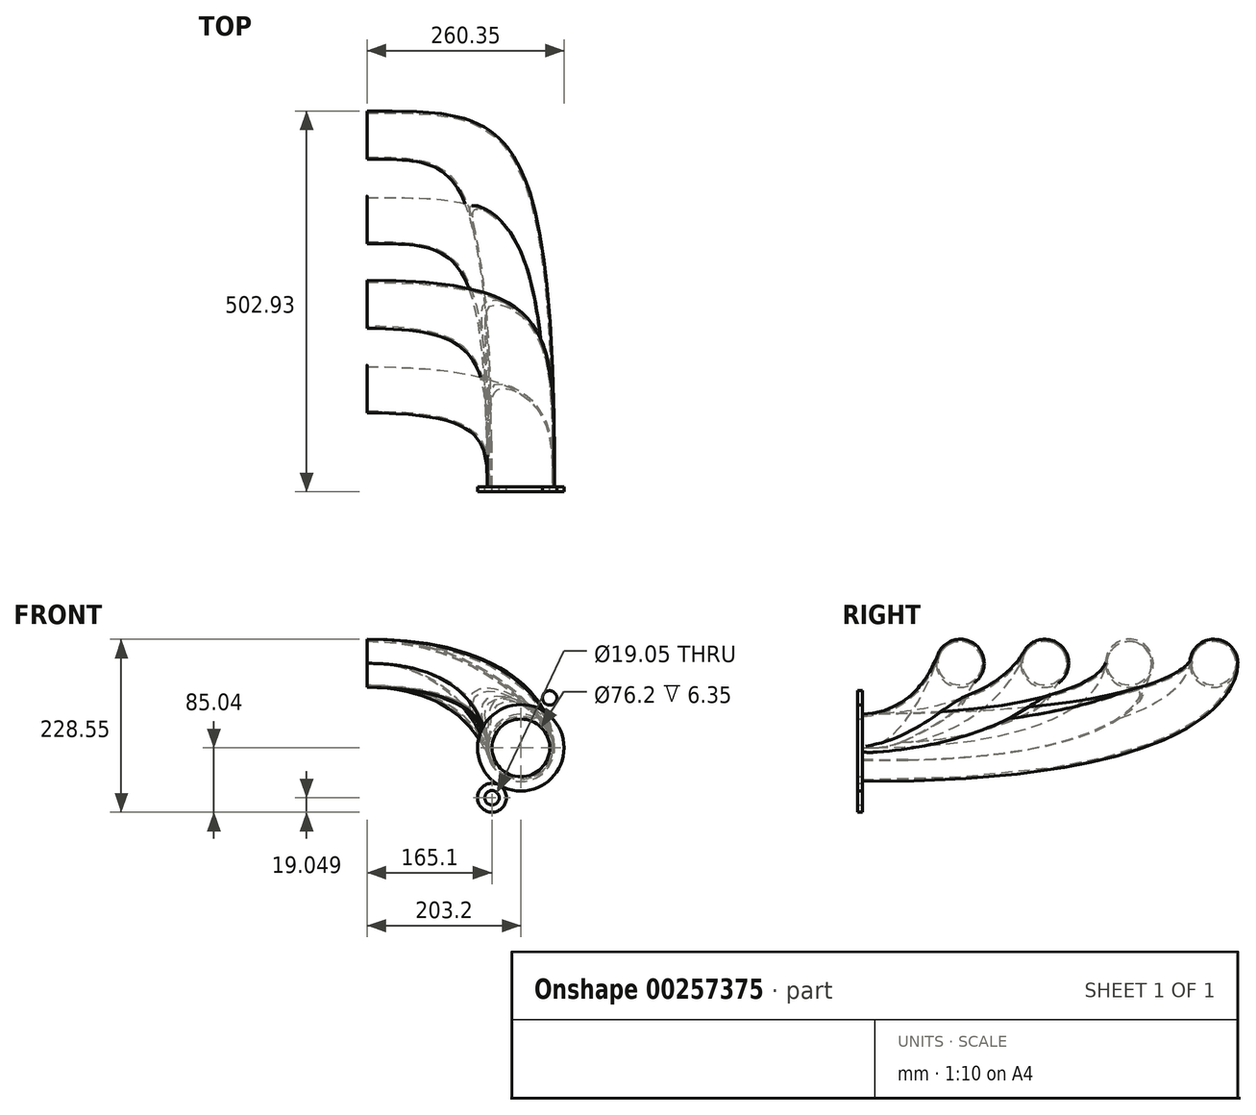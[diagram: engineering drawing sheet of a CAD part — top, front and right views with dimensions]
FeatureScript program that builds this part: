
annotation { "Feature Type Name" : "Feature", "Feature Type Description" : "" }
export const myFeature = defineFeature(function(context is Context, id is Id, definition is map)
    precondition{}
    {
        {
            var Q0;
            Q0=qCreatedBy(makeId("Right.planeOp"),FACE);
            cPlane(context, id + "F0", {"entities" : qUnion([Q0]), "cplaneType" : CPlaneType.OFFSET, "offset" : 203.2 * mm, "oppositeDirection" : true, "width" : 152.4 * mm, "height" : 152.4 * mm});
        }
        {
            var Q0;
            Q0=qCreatedBy(makeId("Top.planeOp"),FACE);
            cPlane(context, id + "F1", {"entities" : qUnion([Q0]), "cplaneType" : CPlaneType.OFFSET, "offset" : 111.76 * mm, "width" : 152.4 * mm, "height" : 152.4 * mm});
        }
        {
            var Q0;
            Q0=qCreatedBy(makeId("Front.planeOp"),FACE);
            var sketch = newSketch(context, id + "F2", { "sketchPlane" : qUnion([Q0])});
            skCircle(sketch, "E0", {"center": v(0, 0) * mm, "radius": 44.45 * mm});
            skSolve(sketch);
        }
        {
            var Q0;
            Q0=qCreatedBy(id+"F0.planeOp",FACE);
            var sketch = newSketch(context, id + "F3", { "sketchPlane" : qUnion([Q0])});
            skCircle(sketch, "E1", {"center": v(129.54, 111.76) * mm, "radius": 31.75 * mm});
            skCircle(sketch, "E2.1.0.0", {"center": v(241.3, 111.76) * mm, "radius": 31.75 * mm});
            skCircle(sketch, "E2.2.0.0", {"center": v(353.06, 111.76) * mm, "radius": 31.75 * mm});
            skCircle(sketch, "E2.3.0.0", {"center": v(464.82, 111.76) * mm, "radius": 31.75 * mm});
            skLineSegment(sketch, "E2.direction1", {"start": v(129.54, 111.76) * mm, "end": v(241.3, 111.76) * mm, "construction": true});
            skSolve(sketch);
        }
        {
            var Q0;
            Q0=qCreatedBy(makeId("Top.planeOp"),FACE);
            var sketch = newSketch(context, id + "F4", { "sketchPlane" : qUnion([Q0])});
            skLineSegment(sketch, "E3", {"start": v(0, 0) * mm, "end": v(0, -195.45) * mm, "construction": true});
            skSolve(sketch);
        }
        {
            var Q0;
            Q0=qCreatedBy(id+"F1.planeOp",FACE);
            var sketch = newSketch(context, id + "F5", { "sketchPlane" : qUnion([Q0])});
            skLineSegment(sketch, "E4.0", {"start": v(-203.2, 384.81) * mm, "end": v(-203.2, 321.31) * mm, "construction": true});
            skLineSegment(sketch, "E5.0", {"start": v(-203.2, 496.57) * mm, "end": v(-203.2, 433.07) * mm, "construction": true});
            skLineSegment(sketch, "E6.0", {"start": v(-203.2, 273.05) * mm, "end": v(-203.2, 209.55) * mm, "construction": true});
            skLineSegment(sketch, "E7.0", {"start": v(-203.2, 161.3) * mm, "end": v(-203.2, 97.8) * mm, "construction": true});
            skLineSegment(sketch, "E8", {"start": v(-203.2, 97.8) * mm, "end": v(-177.8, 97.8) * mm});
            skLineSegment(sketch, "E9", {"start": v(-203.2, 209.55) * mm, "end": v(-177.8, 209.55) * mm});
            skLineSegment(sketch, "E10", {"start": v(-203.2, 321.31) * mm, "end": v(-177.8, 321.31) * mm});
            skLineSegment(sketch, "E11", {"start": v(-203.2, 433.07) * mm, "end": v(-177.8, 433.07) * mm});
            skSolve(sketch);
        }
        {
            var Q0;
            Q0=qCreatedBy(makeId("Top.planeOp"),FACE);
            var sketch = newSketch(context, id + "F6", { "sketchPlane" : qUnion([Q0])});
            skLineSegment(sketch, "E12.0", {"start": v(44.45, 0) * mm, "end": v(-44.45, 0) * mm, "construction": true});
            skLineSegment(sketch, "E13", {"start": v(-44.45, 0) * mm, "end": v(-44.45, 25.4) * mm});
            skPoint(sketch, "E14", {"position": v(-44.45, 8.03) * mm});
            skSolve(sketch);
        }
        {
            var Q0;
            Q0=qCreatedBy(makeId("Right.planeOp"),FACE);
            cPlane(context, id + "F7", {"entities" : qUnion([Q0]), "cplaneType" : CPlaneType.OFFSET, "offset" : 76.2 * mm, "oppositeDirection" : true, "width" : 152.4 * mm, "height" : 152.4 * mm});
        }
        {
            var Q0;
            Q0=makeQuery(id+"F2.imprint","IMPRINT",FACE,{"disambiguationData":[TD([[makeQuery(id+"F2.imprint","IMPRINT",EDGE,{"derivedFrom":sQuery(id+"F2.wireOp",EDGE,"E0")}),1.0]])]});
            var Q1;
            Q1=makeQuery(id+"F3.imprint","IMPRINT",FACE,{"disambiguationData":[TD([[makeQuery(id+"F3.imprint","IMPRINT",EDGE,{"derivedFrom":sQuery(id+"F3.wireOp",EDGE,"E1")}),1.0]])]});
            var Q2;
            Q2=sQuery(id+"F6.wireOp",VERTEX,"E13.start");
            var Q3;
            Q3=sQuery(id+"F5.wireOp",VERTEX,"E8.start");
            loft(context, id + "F8", {"startCondition" : LoftEndDerivativeType.NORMAL_TO_PROFILE, "startMagnitude" : 1.6, "endCondition" : LoftEndDerivativeType.NORMAL_TO_PROFILE, "endMagnitude" : 2.9, "sheetProfilesArray" : [{ "sheetProfileEntities" : qUnion([Q0]) }, { "sheetProfileEntities" : qUnion([Q1]) }], "matchConnections" : true, "connections" : [{ "connectionEntities" : qUnion([Q2, Q3]), "connectionEdgeQueries" : qUnion([]), "connectionEdgeParameters" : [] }]});
        }
        {
            var Q0;
            Q0=makeQuery(id+"F2.imprint","IMPRINT",FACE,{"disambiguationData":[TD([[makeQuery(id+"F2.imprint","IMPRINT",EDGE,{"derivedFrom":sQuery(id+"F2.wireOp",EDGE,"E0")}),1.0]])]});
            var Q1;
            Q1=makeQuery(id+"F3.imprint","IMPRINT",FACE,{"disambiguationData":[TD([[makeQuery(id+"F3.imprint","IMPRINT",EDGE,{"derivedFrom":sQuery(id+"F3.wireOp",EDGE,"E2.1.0.0")}),1.0]])]});
            var Q2;
            Q2=sQuery(id+"F6.wireOp",VERTEX,"E13.start");
            var Q3;
            Q3=sQuery(id+"F5.wireOp",VERTEX,"E9.start");
            loft(context, id + "F9", {"operationType" : NewBodyOperationType.ADD, "startCondition" : LoftEndDerivativeType.NORMAL_TO_PROFILE, "startMagnitude" : 2.2, "endCondition" : LoftEndDerivativeType.NORMAL_TO_PROFILE, "endMagnitude" : 2.9, "sheetProfilesArray" : [{ "sheetProfileEntities" : qUnion([Q0]) }, { "sheetProfileEntities" : qUnion([Q1]) }], "matchConnections" : true, "connections" : [{ "connectionEntities" : qUnion([Q2, Q3]), "connectionEdgeQueries" : qUnion([]), "connectionEdgeParameters" : [] }]});
        }
        {
            var Q0;
            Q0=makeQuery(id+"F2.imprint","IMPRINT",FACE,{"disambiguationData":[TD([[makeQuery(id+"F2.imprint","IMPRINT",EDGE,{"derivedFrom":sQuery(id+"F2.wireOp",EDGE,"E0")}),1.0]])]});
            var Q1;
            Q1=makeQuery(id+"F3.imprint","IMPRINT",FACE,{"disambiguationData":[TD([[makeQuery(id+"F3.imprint","IMPRINT",EDGE,{"derivedFrom":sQuery(id+"F3.wireOp",EDGE,"E2.2.0.0")}),1.0]])]});
            var Q2;
            Q2=sQuery(id+"F6.wireOp",VERTEX,"E13.start");
            var Q3;
            Q3=sQuery(id+"F5.wireOp",VERTEX,"E10.start");
            loft(context, id + "F10", {"operationType" : NewBodyOperationType.ADD, "startCondition" : LoftEndDerivativeType.NORMAL_TO_PROFILE, "startMagnitude" : 3, "endCondition" : LoftEndDerivativeType.NORMAL_TO_PROFILE, "endMagnitude" : 2, "sheetProfilesArray" : [{ "sheetProfileEntities" : qUnion([Q0]) }, { "sheetProfileEntities" : qUnion([Q1]) }], "matchConnections" : true, "connections" : [{ "connectionEntities" : qUnion([Q2, Q3]), "connectionEdgeQueries" : qUnion([]), "connectionEdgeParameters" : [] }]});
        }
        {
            var Q0;
            Q0=makeQuery(id+"F2.imprint","IMPRINT",FACE,{"disambiguationData":[TD([[makeQuery(id+"F2.imprint","IMPRINT",EDGE,{"derivedFrom":sQuery(id+"F2.wireOp",EDGE,"E0")}),1.0]])]});
            var Q1;
            Q1=makeQuery(id+"F3.imprint","IMPRINT",FACE,{"disambiguationData":[TD([[makeQuery(id+"F3.imprint","IMPRINT",EDGE,{"derivedFrom":sQuery(id+"F3.wireOp",EDGE,"E2.3.0.0")}),1.0]])]});
            var Q2;
            Q2=sQuery(id+"F6.wireOp",VERTEX,"E13.start");
            var Q3;
            Q3=sQuery(id+"F5.wireOp",VERTEX,"E5.0.end");
            loft(context, id + "F11", {"operationType" : NewBodyOperationType.ADD, "startCondition" : LoftEndDerivativeType.NORMAL_TO_PROFILE, "startMagnitude" : 3, "endCondition" : LoftEndDerivativeType.NORMAL_TO_PROFILE, "endMagnitude" : 2, "sheetProfilesArray" : [{ "sheetProfileEntities" : qUnion([Q0]) }, { "sheetProfileEntities" : qUnion([Q1]) }], "matchConnections" : true, "connections" : [{ "connectionEntities" : qUnion([Q2, Q3]), "connectionEdgeQueries" : qUnion([]), "connectionEdgeParameters" : [] }]});
        }
        {
            var Q0;
            Q0=makeQuery(id+"F2.imprint","IMPRINT",FACE,{"disambiguationData":[TD([[makeQuery(id+"F2.imprint","IMPRINT",EDGE,{"derivedFrom":sQuery(id+"F2.wireOp",EDGE,"E0")}),1.0]])]});
            var sketch = newSketch(context, id + "F12", { "sketchPlane" : qUnion([Q0])});
            skCircle(sketch, "E15", {"center": v(0, 0) * mm, "radius": 38.1 * mm});
            skCircle(sketch, "E16", {"center": v(0, 0) * mm, "radius": 57.15 * mm});
            skCircle(sketch, "E17", {"center": v(38.1, 66) * mm, "radius": 19.05 * mm});
            skCircle(sketch, "E18", {"center": v(38.1, 66) * mm, "radius": 9.53 * mm});
            skCircle(sketch, "E19", {"center": v(9.52, 66) * mm, "radius": 9.53 * mm});
            skCircle(sketch, "E20", {"center": v(52.39, 41.24) * mm, "radius": 9.53 * mm});
            skCircle(sketch, "E21.MirrorC", {"center": v(9.53, 66) * mm, "radius": 9.53 * mm});
            skCircle(sketch, "E22", {"center": v(-38.1, -66) * mm, "radius": 19.05 * mm});
            skCircle(sketch, "E23", {"center": v(-52.39, -41.24) * mm, "radius": 9.53 * mm});
            skCircle(sketch, "E24", {"center": v(-9.52, -66) * mm, "radius": 9.53 * mm});
            skCircle(sketch, "E25", {"center": v(-38.1, -66) * mm, "radius": 9.53 * mm});
            skLineSegment(sketch, "E26", {"start": v(38.1, 66) * mm, "end": v(0, 0) * mm, "construction": true});
            skSolve(sketch);
        }
        {
            var Q0;
            Q0=makeQuery(id+"F8.opLoft","CAP_FACE",FACE,{"disambiguationData":[OSD([makeQuery(id+"F2.imprint","IMPRINT",FACE,{"disambiguationData":[TD([[makeQuery(id+"F2.imprint","IMPRINT",EDGE,{"derivedFrom":sQuery(id+"F2.wireOp",EDGE,"E0")}),1.0]])]})])],"isStart":true});
            var Q1;
            Q1=makeQuery(id+"F8.opLoft","CAP_FACE",FACE,{"disambiguationData":[OSD([makeQuery(id+"F3.imprint","IMPRINT",FACE,{"disambiguationData":[TD([[makeQuery(id+"F3.imprint","IMPRINT",EDGE,{"derivedFrom":sQuery(id+"F3.wireOp",EDGE,"E1")}),1.0]])]})])],"isStart":true});
            var Q2;
            Q2=makeQuery(id+"F11.opLoft","CAP_FACE",FACE,{"disambiguationData":[OSD([makeQuery(id+"F3.imprint","IMPRINT",FACE,{"disambiguationData":[TD([[makeQuery(id+"F3.imprint","IMPRINT",EDGE,{"derivedFrom":sQuery(id+"F3.wireOp",EDGE,"E2.3.0.0")}),1.0]])]})])],"isStart":true});
            var Q3;
            Q3=makeQuery(id+"F10.opLoft","CAP_FACE",FACE,{"disambiguationData":[OSD([makeQuery(id+"F3.imprint","IMPRINT",FACE,{"disambiguationData":[TD([[makeQuery(id+"F3.imprint","IMPRINT",EDGE,{"derivedFrom":sQuery(id+"F3.wireOp",EDGE,"E2.2.0.0")}),1.0]])]})])],"isStart":true});
            var Q4;
            Q4=makeQuery(id+"F9.opLoft","CAP_FACE",FACE,{"disambiguationData":[OSD([makeQuery(id+"F3.imprint","IMPRINT",FACE,{"disambiguationData":[TD([[makeQuery(id+"F3.imprint","IMPRINT",EDGE,{"derivedFrom":sQuery(id+"F3.wireOp",EDGE,"E2.1.0.0")}),1.0]])]})])],"isStart":true});
            shell(context, id + "F13", {"entities" : qUnion([Q0, Q1, Q2, Q3, Q4]), "thickness" : 2.54 * mm});
        }
        {
            var Q0;
            Q0=makeQuery(id+"F12.imprint","IMPRINT",FACE,{"disambiguationData":[TD([[makeQuery(id+"F12.imprint","IMPRINT",EDGE,{"derivedFrom":makeQuery(id+"F2.imprint","IMPRINT",EDGE,{"derivedFrom":sQuery(id+"F2.wireOp",EDGE,"E0")})}),-1.0]])]});
            var Q1;
            Q1=makeQuery(id+"F12.imprint","IMPRINT",FACE,{"disambiguationData":[TD([[makeQuery(id+"F12.imprint","IMPRINT",EDGE,{"derivedFrom":sQuery(id+"F12.wireOp",EDGE,"E15")}),-1.0]])]});
            var Q2;
            {var subQ0=sQuery(id+"F12.wireOp",EDGE,"E16");var subQ1=sQuery(id+"F12.wireOp",EDGE,"E21.MirrorC");var subQ2=makeQuery(id+"F12.imprint","INTERSECT",VERTEX,{"derivedFrom":[subQ1,subQ0]});Q2=makeQuery(id+"F12.imprint","IMPRINT",FACE,{"disambiguationData":[TD([[makeQuery(id+"F12.imprint","IMPRINT",EDGE,{"disambiguationData":[TD([[subQ2,1.0]])],"derivedFrom":subQ1}),1.0]])]});}
            var Q3;
            {var subQ0=sQuery(id+"F12.wireOp",EDGE,"E16");var subQ1=sQuery(id+"F12.wireOp",EDGE,"E20");var subQ2=makeQuery(id+"F12.imprint","INTERSECT",VERTEX,{"derivedFrom":[subQ1,subQ0]});Q3=makeQuery(id+"F12.imprint","IMPRINT",FACE,{"disambiguationData":[TD([[makeQuery(id+"F12.imprint","IMPRINT",EDGE,{"disambiguationData":[TD([[subQ2,-1.0]])],"derivedFrom":subQ1}),1.0]])]});}
            var Q4;
            Q4=makeQuery(id+"F12.imprint","IMPRINT",FACE,{"disambiguationData":[TD([[makeQuery(id+"F12.imprint","IMPRINT",EDGE,{"derivedFrom":sQuery(id+"F12.wireOp",EDGE,"E18")}),1.0]])]});
            var Q5;
            Q5=makeQuery(id+"F12.imprint","IMPRINT",FACE,{"disambiguationData":[TD([[makeQuery(id+"F12.imprint","IMPRINT",EDGE,{"derivedFrom":sQuery(id+"F12.wireOp",EDGE,"E25")}),-1.0]])]});
            var Q6;
            {var subQ0=sQuery(id+"F12.wireOp",EDGE,"E23");var subQ1=sQuery(id+"F12.wireOp",EDGE,"E16");var subQ2=makeQuery(id+"F12.imprint","INTERSECT",VERTEX,{"derivedFrom":[subQ1,subQ0]});Q6=makeQuery(id+"F12.imprint","IMPRINT",FACE,{"disambiguationData":[TD([[makeQuery(id+"F12.imprint","IMPRINT",EDGE,{"disambiguationData":[TD([[subQ2,1.0]])],"derivedFrom":subQ1}),1.0]])]});}
            var Q7;
            {var subQ0=sQuery(id+"F12.wireOp",EDGE,"E24");var subQ1=sQuery(id+"F12.wireOp",EDGE,"E16");var subQ2=makeQuery(id+"F12.imprint","INTERSECT",VERTEX,{"derivedFrom":[subQ1,subQ0]});Q7=makeQuery(id+"F12.imprint","IMPRINT",FACE,{"disambiguationData":[TD([[makeQuery(id+"F12.imprint","IMPRINT",EDGE,{"disambiguationData":[TD([[subQ2,-1.0]])],"derivedFrom":subQ1}),1.0]])]});}
            extrude(context, id + "F14", {"entities" : qUnion([Q0, Q1, Q2, Q3, Q4, Q5, Q6, Q7]), "operationType" : NewBodyOperationType.ADD, "depth" : 6.35 * mm});
        }
    });
